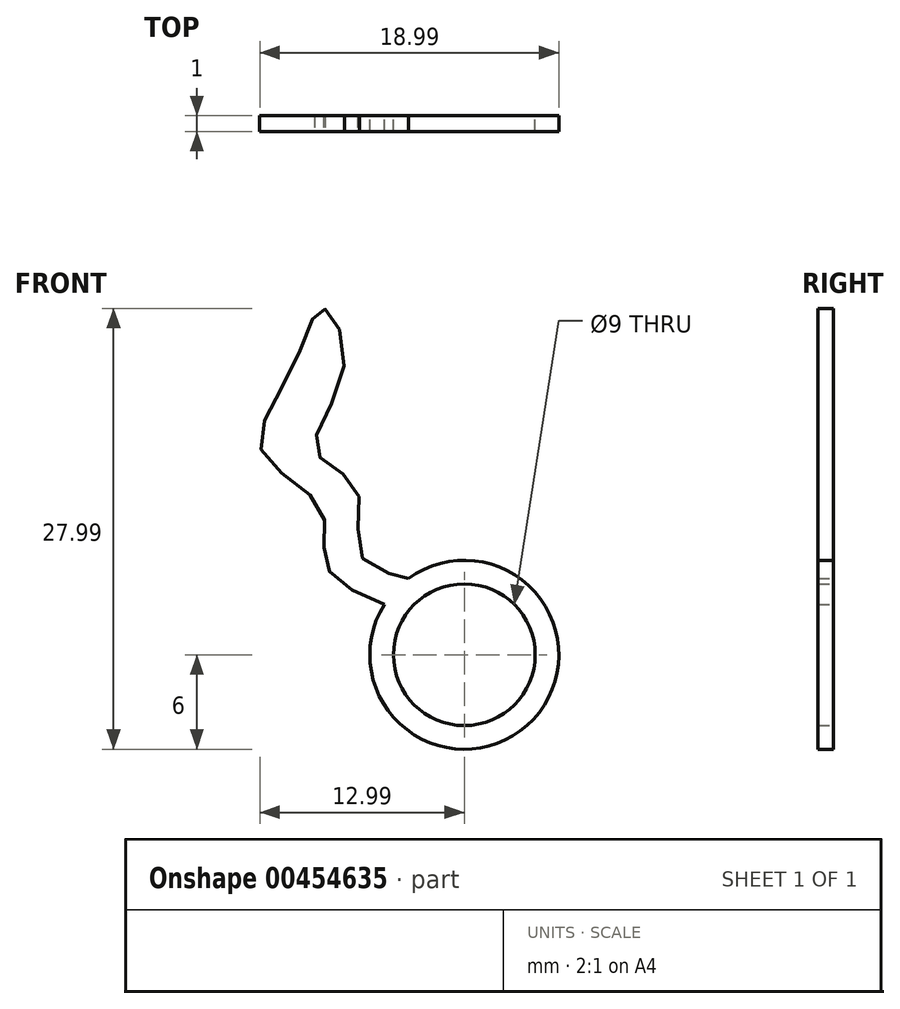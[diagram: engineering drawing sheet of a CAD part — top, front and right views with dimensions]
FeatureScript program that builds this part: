
annotation { "Feature Type Name" : "Feature", "Feature Type Description" : "" }
export const myFeature = defineFeature(function(context is Context, id is Id, definition is map)
    precondition{}
    {
        {
            var Q0;
            Q0=qCreatedBy(makeId("Front.planeOp"),FACE);
            var sketch = newSketch(context, id + "F0", { "sketchPlane" : qUnion([Q0])});
            skCircle(sketch, "E0", {"center": v(0, 0) * mm, "radius": 4.5 * mm});
            skCircle(sketch, "E1", {"center": v(0, 0) * mm, "radius": 6 * mm});
            skFitSpline(sketch, "E2", {"points": [v(-5.08, 3.19) * mm, v(-8.82, 5.77) * mm, v(-9.1, 9.28) * mm, v(-12.88, 12.98) * mm, v(-10.8, 18.47) * mm, v(-9, 21.99) * mm, v(-7.65, 18.3) * mm, v(-9.45, 12.98) * mm, v(-6.84, 10.55) * mm, v(-6.39, 6.04) * mm, v(-3.53, 4.85) * mm, v(-3.58, 4.81) * mm], "startDerivative": vector(-49.71, 21.07) * mm, "endDerivative": vector(-8.37, -1.31) * mm});
            skSolve(sketch);
        }
        {
            var Q0;
            Q0 = qSketchRegion(id + "F0", true);
            extrude(context, id + "F1", {"entities" : qUnion([Q0]), "depth" : 1 * mm});
        }
    });
